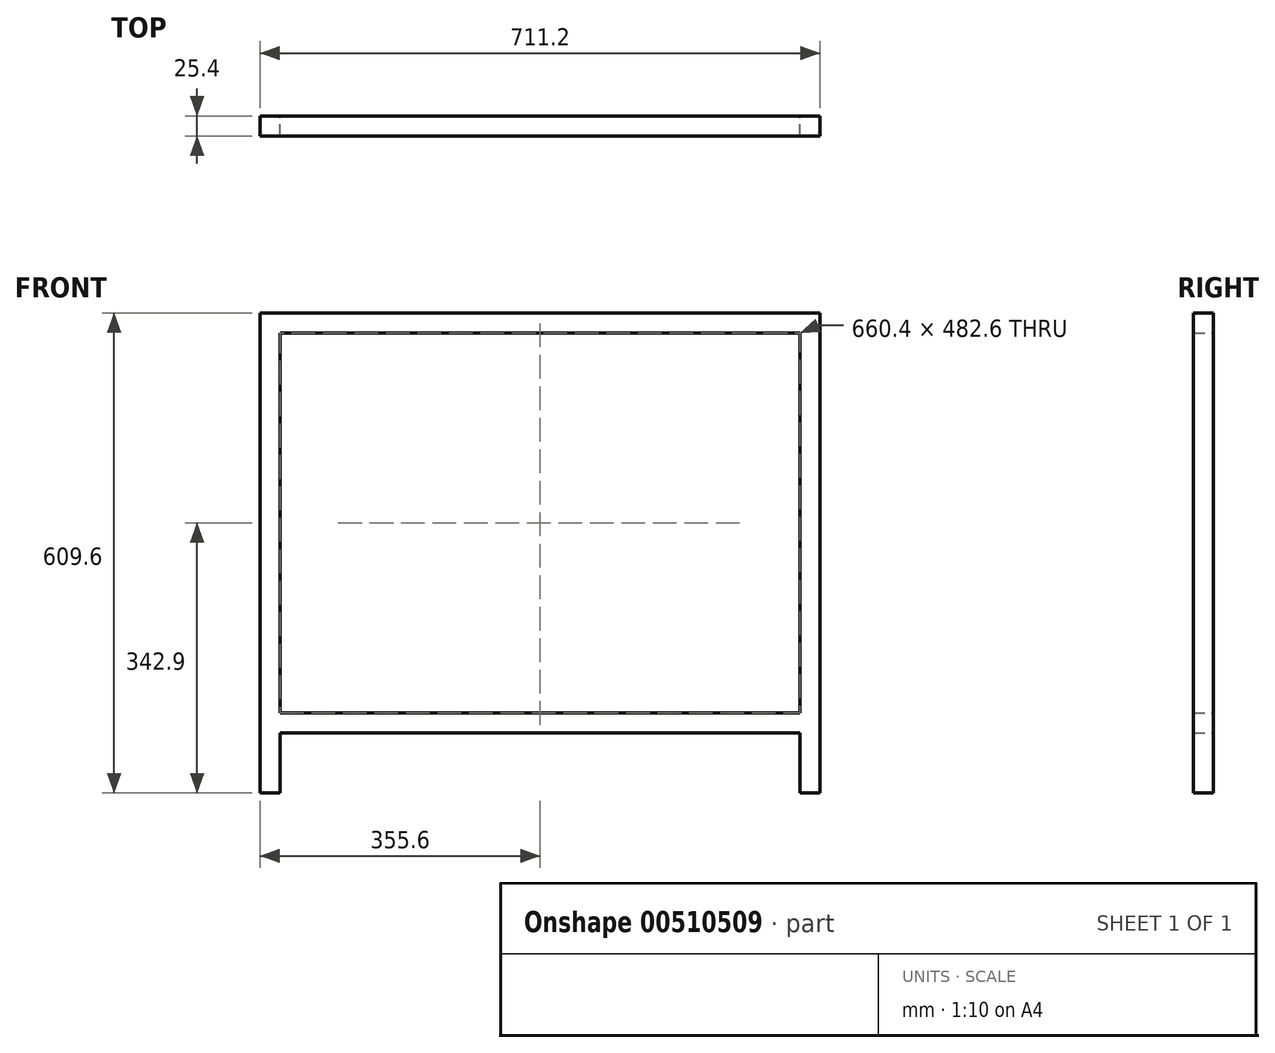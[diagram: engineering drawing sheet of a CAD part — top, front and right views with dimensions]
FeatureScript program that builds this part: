
annotation { "Feature Type Name" : "Feature", "Feature Type Description" : "" }
export const myFeature = defineFeature(function(context is Context, id is Id, definition is map)
    precondition{}
    {
        {
            var Q0;
            Q0=qCreatedBy(makeId("Front.planeOp"),FACE);
            var sketch = newSketch(context, id + "F0", { "sketchPlane" : qUnion([Q0])});
            skLineSegment(sketch, "E0.bottom", {"start": v(-355.6, 304.8) * mm, "end": v(-330.2, 304.8) * mm});
            skLineSegment(sketch, "E0.top", {"start": v(-355.6, -304.8) * mm, "end": v(-330.2, -304.8) * mm});
            skLineSegment(sketch, "E0.left", {"start": v(-355.6, 304.8) * mm, "end": v(-355.6, -304.8) * mm});
            skLineSegment(sketch, "E0.right", {"start": v(-330.2, 304.8) * mm, "end": v(-330.2, -304.8) * mm});
            skLineSegment(sketch, "E1.bottom", {"start": v(-330.2, 304.8) * mm, "end": v(0, 304.8) * mm});
            skLineSegment(sketch, "E1.top", {"start": v(-330.2, 279.4) * mm, "end": v(0, 279.4) * mm});
            skLineSegment(sketch, "E1.left", {"start": v(-330.2, 304.8) * mm, "end": v(-330.2, 279.4) * mm});
            skLineSegment(sketch, "E2", {"start": v(0, 304.8) * mm, "end": v(0, -304.8) * mm, "construction": true});
            skPoint(sketch, "E3", {"position": v(0, 0) * mm});
            skLineSegment(sketch, "E4.bottom", {"start": v(-330.2, -203.2) * mm, "end": v(0, -203.2) * mm});
            skLineSegment(sketch, "E4.top", {"start": v(-330.2, -228.6) * mm, "end": v(0, -228.6) * mm});
            skLineSegment(sketch, "E4.left", {"start": v(-330.2, -203.2) * mm, "end": v(-330.2, -228.6) * mm});
            skLineSegment(sketch, "E4.right", {"start": v(0, -203.2) * mm, "end": v(0, -228.6) * mm});
            skPoint(sketch, "E5", {"position": v(0, 279.4) * mm});
            skLineSegment(sketch, "E6", {"start": v(0, 279.4) * mm, "end": v(0, 304.8) * mm});
            skLineSegment(sketch, "E7.MirrorCS", {"start": v(330.2, -228.6) * mm, "end": v(0, -228.6) * mm});
            skLineSegment(sketch, "E8.MirrorCS", {"start": v(355.6, 304.8) * mm, "end": v(355.6, -304.8) * mm});
            skLineSegment(sketch, "E9.MirrorCS", {"start": v(330.2, 304.8) * mm, "end": v(330.2, -304.8) * mm});
            skLineSegment(sketch, "E10.MirrorCS", {"start": v(330.2, 279.4) * mm, "end": v(0, 279.4) * mm});
            skLineSegment(sketch, "E11.MirrorCS", {"start": v(330.2, 304.8) * mm, "end": v(0, 304.8) * mm});
            skLineSegment(sketch, "E12.MirrorCS", {"start": v(355.6, -304.8) * mm, "end": v(330.2, -304.8) * mm});
            skLineSegment(sketch, "E13.MirrorCS", {"start": v(330.2, -203.2) * mm, "end": v(0, -203.2) * mm});
            skLineSegment(sketch, "E14.MirrorCS", {"start": v(355.6, 304.8) * mm, "end": v(330.2, 304.8) * mm});
            skSolve(sketch);
        }
        {
            var Q0;
            Q0=sQuery(id+"F0.wireOp",EDGE,"E11.MirrorCS");
            var Q1;
            Q1 = qSketchRegion(id + "F0", true);
            extrude(context, id + "F1", {"bodyType" : ToolBodyType.SURFACE, "surfaceEntities" : qUnion([Q0, Q1]), "depth" : 25.4 * mm});
        }
    });
